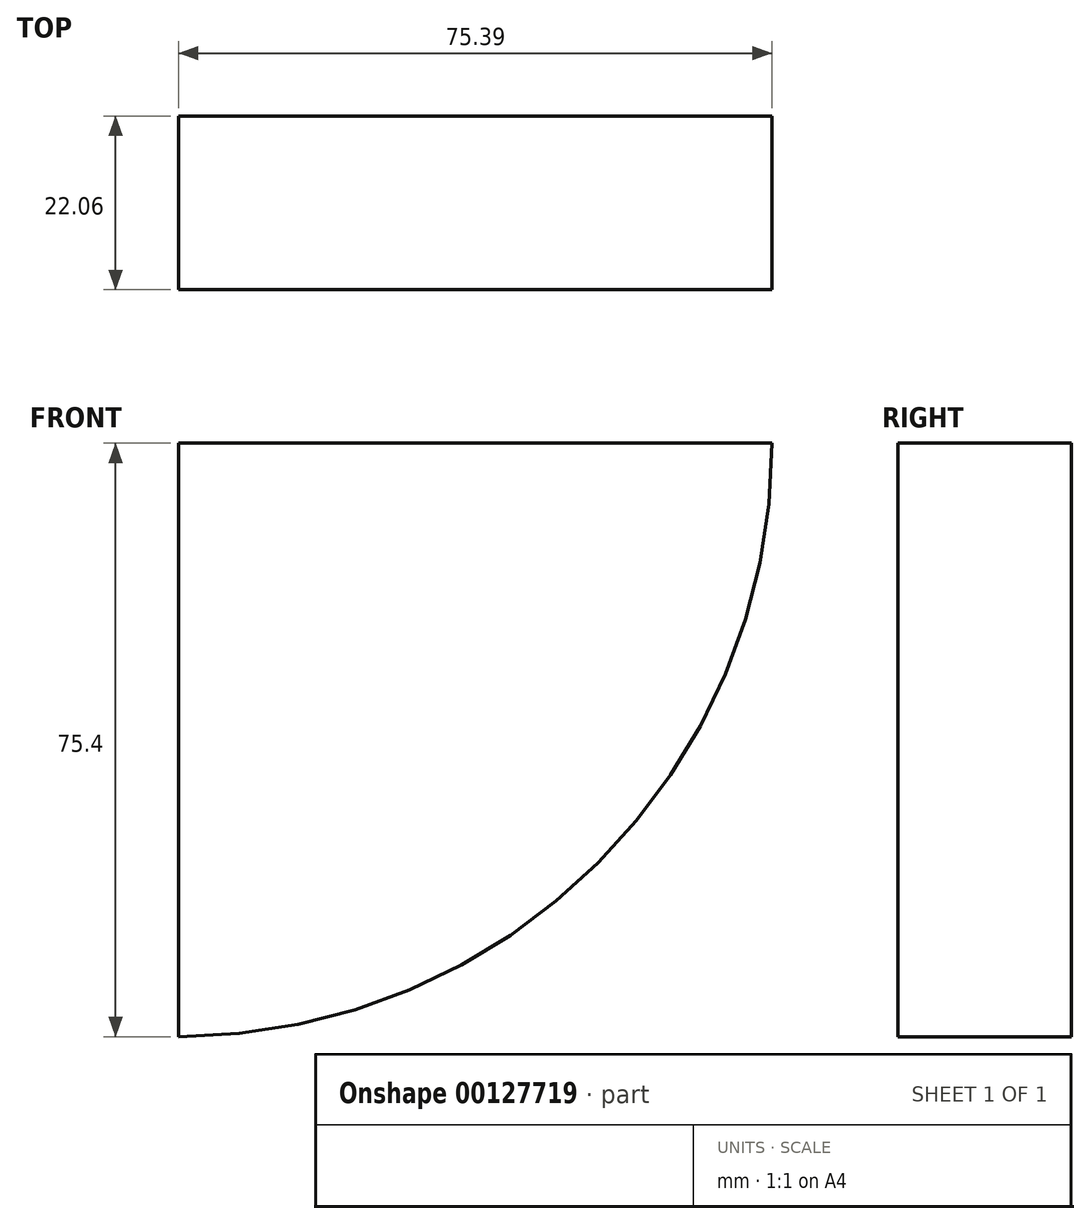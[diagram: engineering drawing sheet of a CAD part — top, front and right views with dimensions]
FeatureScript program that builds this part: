
annotation { "Feature Type Name" : "Feature", "Feature Type Description" : "" }
export const myFeature = defineFeature(function(context is Context, id is Id, definition is map)
    precondition{}
    {
        {
            var Q0;
            Q0=qCreatedBy(makeId("Right.planeOp"),FACE);
            var sketch = newSketch(context, id + "F0", { "sketchPlane" : qUnion([Q0])});
            skLineSegment(sketch, "E0.bottom", {"start": v(11.03, 37.7) * mm, "end": v(-11.03, 37.7) * mm});
            skLineSegment(sketch, "E0.top", {"start": v(11.03, -37.7) * mm, "end": v(-11.03, -37.7) * mm});
            skLineSegment(sketch, "E0.left", {"start": v(11.03, 37.7) * mm, "end": v(11.03, -37.7) * mm});
            skLineSegment(sketch, "E0.right", {"start": v(-11.03, 37.7) * mm, "end": v(-11.03, -37.7) * mm});
            skPoint(sketch, "E0.middle", {"position": v(0, 0) * mm});
            skSolve(sketch);
        }
        {
            var Q0;
            Q0 = qSketchRegion(id + "F0", true);
            var Q1;
            Q1=sQuery(id+"F0.wireOp",EDGE,"E0.bottom");
            revolve(context, id + "F1", {"entities" : qUnion([Q0]), "axis" : qUnion([Q1]), "revolveType" : RevolveType.ONE_DIRECTION, "angle" : 90 * degree});
        }
    });
